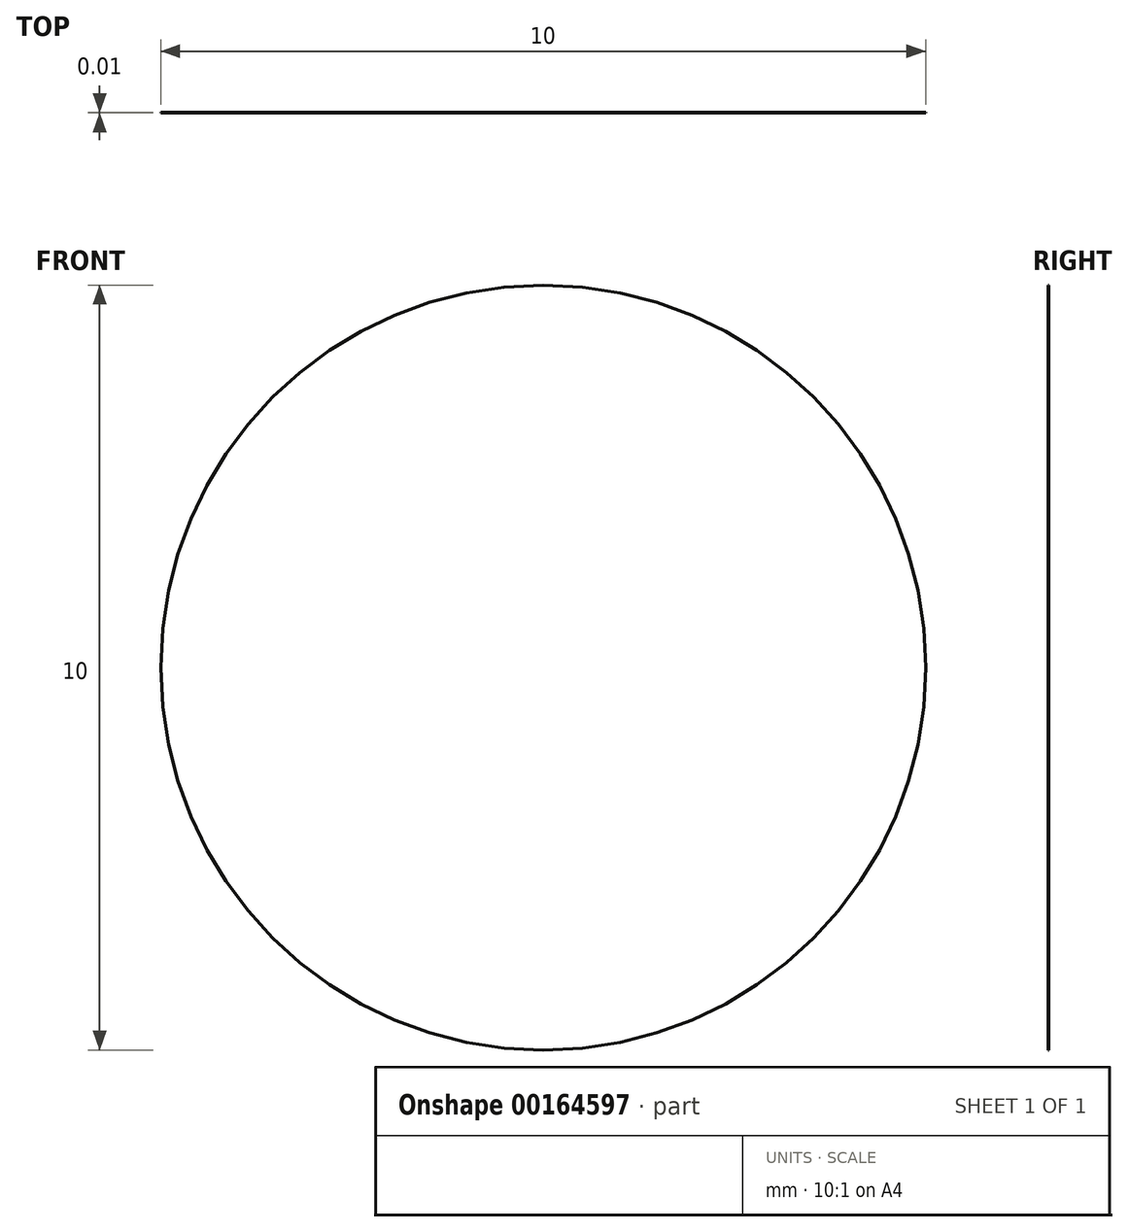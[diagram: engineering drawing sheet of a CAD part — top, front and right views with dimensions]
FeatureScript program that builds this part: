
annotation { "Feature Type Name" : "Feature", "Feature Type Description" : "" }
export const myFeature = defineFeature(function(context is Context, id is Id, definition is map)
    precondition{}
    {
        {
            var Q0;
            Q0=qCreatedBy(makeId("Front.planeOp"),FACE);
            var sketch = newSketch(context, id + "F0", { "sketchPlane" : qUnion([Q0])});
            skCircle(sketch, "E0", {"center": v(0, 0) * mm, "radius": 5 * mm});
            skSolve(sketch);
        }
        {
            var Q0;
            Q0=makeQuery(id+"F0.imprint","IMPRINT",FACE,{"disambiguationData":[TD([[makeQuery(id+"F0.imprint","IMPRINT",EDGE,{"derivedFrom":sQuery(id+"F0.wireOp",EDGE,"E0")}),1.0]])]});
            extrude(context, id + "F1", {"entities" : qUnion([Q0]), "oppositeDirection" : true, "depth" : 0.01 * mm});
        }
    });
